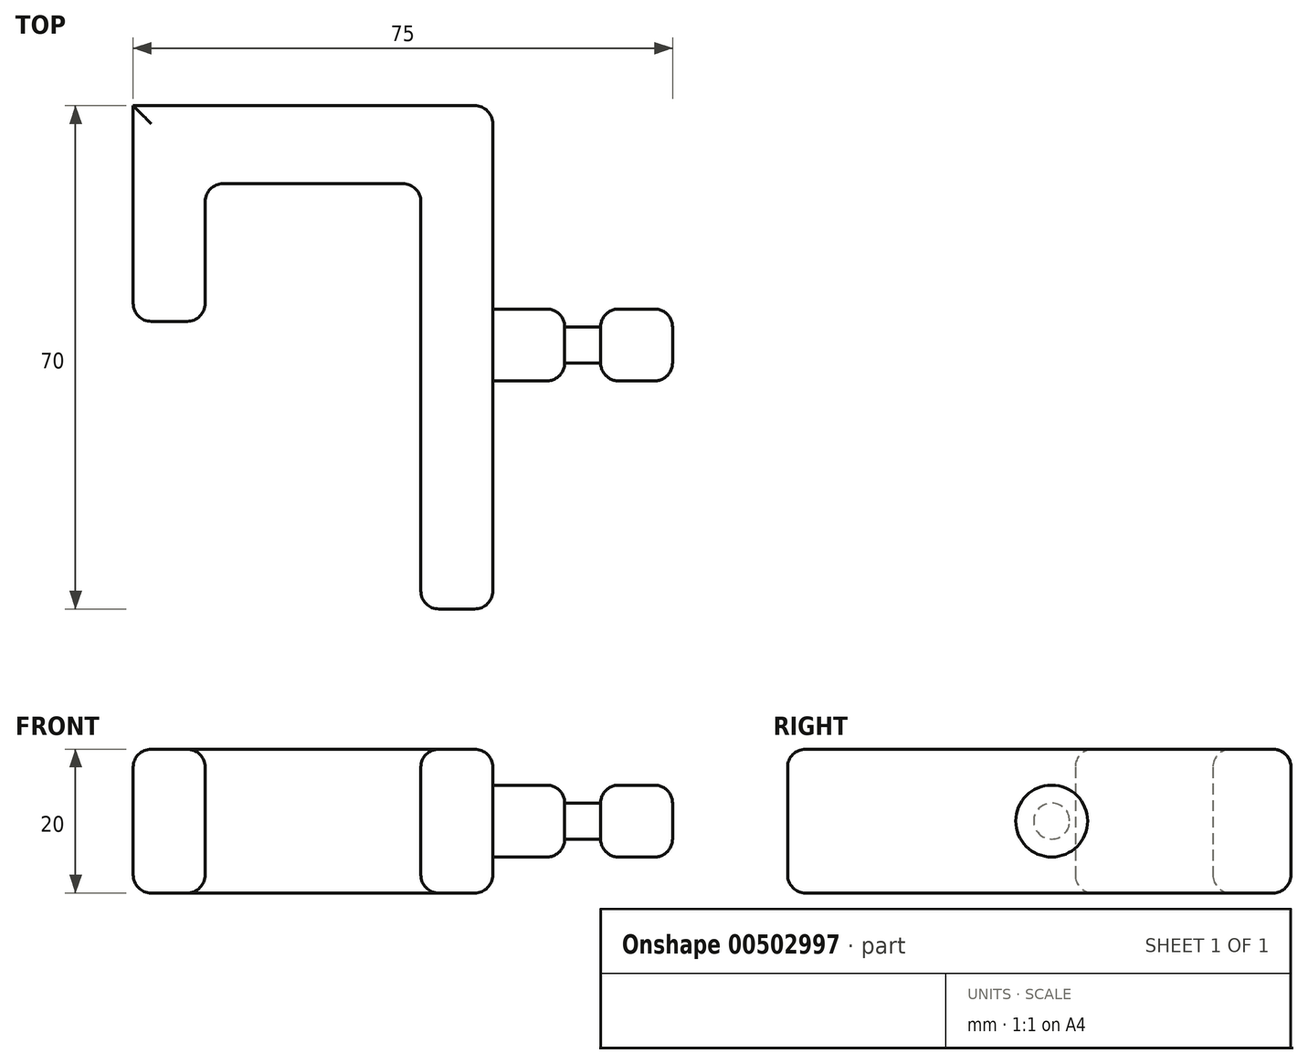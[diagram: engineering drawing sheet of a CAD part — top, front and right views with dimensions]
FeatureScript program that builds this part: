
annotation { "Feature Type Name" : "Feature", "Feature Type Description" : "" }
export const myFeature = defineFeature(function(context is Context, id is Id, definition is map)
    precondition{}
    {
        {
            var Q0;
            Q0=qCreatedBy(makeId("Top.planeOp"),FACE);
            var sketch = newSketch(context, id + "F0", { "sketchPlane" : qUnion([Q0])});
            skLineSegment(sketch, "E0.bottom", {"start": v(-50, 33.27) * mm, "end": v(-40, 33.27) * mm});
            skLineSegment(sketch, "E0.top", {"start": v(-50, 3.27) * mm, "end": v(-40, 3.27) * mm});
            skLineSegment(sketch, "E0.left", {"start": v(-50, 33.27) * mm, "end": v(-50, 3.27) * mm});
            skLineSegment(sketch, "E0.right", {"start": v(-40, 33.27) * mm, "end": v(-40, 3.27) * mm});
            skLineSegment(sketch, "E1.bottom", {"start": v(-50, 33.27) * mm, "end": v(0, 33.27) * mm});
            skLineSegment(sketch, "E1.top", {"start": v(-50, 22.42) * mm, "end": v(0, 22.42) * mm});
            skLineSegment(sketch, "E1.left", {"start": v(-50, 33.27) * mm, "end": v(-50, 22.42) * mm});
            skLineSegment(sketch, "E1.right", {"start": v(0, 33.27) * mm, "end": v(0, 22.42) * mm});
            skLineSegment(sketch, "E2.bottom", {"start": v(0, 33.27) * mm, "end": v(-10, 33.27) * mm});
            skLineSegment(sketch, "E2.top", {"start": v(0, -36.73) * mm, "end": v(-10, -36.73) * mm});
            skLineSegment(sketch, "E2.left", {"start": v(0, 33.27) * mm, "end": v(0, -36.73) * mm});
            skLineSegment(sketch, "E2.right", {"start": v(-10, 33.27) * mm, "end": v(-10, -36.73) * mm});
            skSolve(sketch);
        }
        {
            var Q0;
            Q0 = qSketchRegion(id + "F0", true);
            extrude(context, id + "F1", {"entities" : qUnion([Q0]), "depth" : 20 * mm});
        }
        {
            var Q0;
            Q0=makeQuery(id+"F1.opExtrude","SWEPT_FACE",FACE,{"disambiguationData":[OSD([sQuery(id+"F0.wireOp",EDGE,"E2.left")])]});
            var sketch = newSketch(context, id + "F2", { "sketchPlane" : qUnion([Q0])});
            skCircle(sketch, "E3", {"center": v(0, 10) * mm, "radius": 5 * mm});
            skSolve(sketch);
        }
        {
            var Q0;
            Q0=makeQuery(id+"F2.imprint","IMPRINT",FACE,{"disambiguationData":[TD([[makeQuery(id+"F2.imprint","IMPRINT",EDGE,{"derivedFrom":sQuery(id+"F2.wireOp",EDGE,"E3")}),1.0]])]});
            extrude(context, id + "F3", {"entities" : qUnion([Q0]), "operationType" : NewBodyOperationType.ADD, "depth" : 10 * mm});
        }
        {
            var Q0;
            Q0=makeQuery(id+"F3.opExtrude","CAP_FACE",FACE,{"disambiguationData":[OSD([sQuery(id+"F2.wireOp",EDGE,"E3")])],"isStart":false});
            var sketch = newSketch(context, id + "F4", { "sketchPlane" : qUnion([Q0])});
            skSolve(sketch);
        }
        {
            var Q0;
            Q0=makeQuery(id+"F4.imprint","IMPRINT",FACE,{"disambiguationData":[TD([[makeQuery(id+"F4.imprint","IMPRINT",EDGE,{"derivedFrom":makeQuery(id+"F3.opExtrude","CAP_EDGE",EDGE,{"disambiguationData":[OSD([sQuery(id+"F2.wireOp",EDGE,"E3")])],"isStart":false})}),1.0]])]});
            var sketch = newSketch(context, id + "F5", { "sketchPlane" : qUnion([Q0])});
            skCircle(sketch, "E4", {"center": v(0, 10) * mm, "radius": 2.5 * mm});
            skSolve(sketch);
        }
        {
            var Q0;
            Q0=makeQuery(id+"F5.imprint","IMPRINT",FACE,{"disambiguationData":[TD([[makeQuery(id+"F5.imprint","IMPRINT",EDGE,{"derivedFrom":sQuery(id+"F5.wireOp",EDGE,"E4")}),1.0]])]});
            extrude(context, id + "F6", {"entities" : qUnion([Q0]), "operationType" : NewBodyOperationType.ADD, "depth" : 5 * mm});
        }
        {
            var Q0;
            Q0=makeQuery(id+"F6.opExtrude","CAP_FACE",FACE,{"disambiguationData":[OSD([sQuery(id+"F5.wireOp",EDGE,"E4")])],"isStart":false});
            var sketch = newSketch(context, id + "F7", { "sketchPlane" : qUnion([Q0])});
            skCircle(sketch, "E5", {"center": v(0, 10) * mm, "radius": 5 * mm});
            skSolve(sketch);
        }
        {
            var Q0;
            Q0=makeQuery(id+"F7.imprint","IMPRINT",FACE,{"disambiguationData":[TD([[makeQuery(id+"F7.imprint","IMPRINT",EDGE,{"derivedFrom":sQuery(id+"F7.wireOp",EDGE,"E5")}),1.0]])]});
            var Q1;
            Q1=makeQuery(id+"F7.imprint","IMPRINT",FACE,{"disambiguationData":[TD([[makeQuery(id+"F7.imprint","IMPRINT",EDGE,{"derivedFrom":makeQuery(id+"F6.opExtrude","CAP_EDGE",EDGE,{"disambiguationData":[OSD([sQuery(id+"F5.wireOp",EDGE,"E4")])],"isStart":false})}),1.0]])]});
            extrude(context, id + "F8", {"entities" : qUnion([Q0, Q1]), "operationType" : NewBodyOperationType.ADD, "depth" : 10 * mm});
        }
        {
            var Q0;
            Q0=makeQuery(id+"F1.opExtrude","SWEPT_EDGE",EDGE,{"disambiguationData":[OSD([sQuery(id+"F0.wireOp",EDGE,"E2.bottom"),sQuery(id+"F0.wireOp",EDGE,"E2.left")])]});
            var Q1;
            Q1=makeQuery(id+"F1.opExtrude","SWEPT_EDGE",EDGE,{"disambiguationData":[OSD([sQuery(id+"F0.wireOp",EDGE,"E1.bottom"),sQuery(id+"F0.wireOp",EDGE,"E1.left")])]});
            var Q2;
            Q2=makeQuery(id+"F1.opExtrude","SWEPT_EDGE",EDGE,{"disambiguationData":[OSD([sQuery(id+"F0.wireOp",EDGE,"E0.top"),sQuery(id+"F0.wireOp",EDGE,"E0.left")])]});
            var Q3;
            Q3=makeQuery(id+"F1.opExtrude","SWEPT_EDGE",EDGE,{"disambiguationData":[OSD([sQuery(id+"F0.wireOp",EDGE,"E0.top"),sQuery(id+"F0.wireOp",EDGE,"E0.right")])]});
            var Q4;
            Q4=makeQuery(id+"F1.opExtrude","SWEPT_EDGE",EDGE,{"disambiguationData":[OSD([sQuery(id+"F0.wireOp",EDGE,"E0.right"),sQuery(id+"F0.wireOp",EDGE,"E1.top")])]});
            var Q5;
            Q5=makeQuery(id+"F1.opExtrude","SWEPT_EDGE",EDGE,{"disambiguationData":[OSD([sQuery(id+"F0.wireOp",EDGE,"E1.top"),sQuery(id+"F0.wireOp",EDGE,"E2.right")])]});
            var Q6;
            Q6=makeQuery(id+"F1.opExtrude","SWEPT_EDGE",EDGE,{"disambiguationData":[OSD([sQuery(id+"F0.wireOp",EDGE,"E2.top"),sQuery(id+"F0.wireOp",EDGE,"E2.right")])]});
            var Q7;
            Q7=makeQuery(id+"F1.opExtrude","SWEPT_EDGE",EDGE,{"disambiguationData":[OSD([sQuery(id+"F0.wireOp",EDGE,"E2.top"),sQuery(id+"F0.wireOp",EDGE,"E2.left")])]});
            var Q8;
            Q8=makeQuery(id+"F1.opExtrude","CAP_EDGE",EDGE,{"disambiguationData":[OSD([sQuery(id+"F0.wireOp",EDGE,"E2.left")])],"isStart":false});
            var Q9;
            Q9=makeQuery(id+"F1.opExtrude","CAP_EDGE",EDGE,{"disambiguationData":[OSD([sQuery(id+"F0.wireOp",EDGE,"E2.right")])],"isStart":false});
            var Q10;
            Q10=makeQuery(id+"F1.opExtrude","CAP_EDGE",EDGE,{"disambiguationData":[OSD([sQuery(id+"F0.wireOp",EDGE,"E1.top")])],"isStart":true});
            var Q11;
            Q11=makeQuery(id+"F1.opExtrude","CAP_EDGE",EDGE,{"disambiguationData":[OSD([sQuery(id+"F0.wireOp",EDGE,"E0.left"),sQuery(id+"F0.wireOp",EDGE,"E1.left")])],"isStart":false});
            var Q12;
            Q12=makeQuery(id+"F1.opExtrude","CAP_EDGE",EDGE,{"disambiguationData":[OSD([sQuery(id+"F0.wireOp",EDGE,"E0.left"),sQuery(id+"F0.wireOp",EDGE,"E1.left")])],"isStart":true});
            var Q13;
            Q13=makeQuery(id+"F1.opExtrude","CAP_EDGE",EDGE,{"disambiguationData":[OSD([sQuery(id+"F0.wireOp",EDGE,"E1.bottom"),sQuery(id+"F0.wireOp",EDGE,"E2.bottom")])],"isStart":true});
            var Q14;
            Q14=makeQuery(id+"F1.opExtrude","CAP_EDGE",EDGE,{"disambiguationData":[OSD([sQuery(id+"F0.wireOp",EDGE,"E1.bottom"),sQuery(id+"F0.wireOp",EDGE,"E2.bottom")])],"isStart":false});
            var Q15;
            Q15=makeQuery(id+"F1.opExtrude","CAP_EDGE",EDGE,{"disambiguationData":[OSD([sQuery(id+"F0.wireOp",EDGE,"E2.left")])],"isStart":true});
            fillet(context, id + "F9", {"entities" : qUnion([Q0, Q1, Q2, Q3, Q4, Q5, Q6, Q7, Q8, Q9, Q10, Q11, Q12, Q13, Q14, Q15]), "radius" : 2.5 * mm, "tangentPropagation" : true, "allowEdgeOverflow" : false});
        }
        {
            var Q0;
            Q0=makeQuery(id+"F1.opExtrude","CAP_EDGE",EDGE,{"disambiguationData":[OSD([sQuery(id+"F0.wireOp",EDGE,"E0.top")])],"isStart":true});
            var Q1;
            Q1=makeQuery(id+"F1.opExtrude","CAP_EDGE",EDGE,{"disambiguationData":[OSD([sQuery(id+"F0.wireOp",EDGE,"E2.top")])],"isStart":true});
            var Q2;
            Q2=makeQuery(id+"F1.opExtrude","CAP_EDGE",EDGE,{"disambiguationData":[OSD([sQuery(id+"F0.wireOp",EDGE,"E2.top")])],"isStart":false});
            var Q3;
            Q3=makeQuery(id+"F3.opExtrude","CAP_EDGE",EDGE,{"disambiguationData":[OSD([sQuery(id+"F2.wireOp",EDGE,"E3")])],"isStart":true});
            var Q4;
            Q4=makeQuery(id+"F8.opExtrude","CAP_EDGE",EDGE,{"disambiguationData":[OSD([sQuery(id+"F7.wireOp",EDGE,"E5")])],"isStart":false});
            var Q5;
            Q5=makeQuery(id+"F3.opExtrude","CAP_EDGE",EDGE,{"disambiguationData":[OSD([sQuery(id+"F2.wireOp",EDGE,"E3")])],"isStart":false});
            var Q6;
            Q6=makeQuery(id+"F8.opExtrude","CAP_EDGE",EDGE,{"disambiguationData":[OSD([sQuery(id+"F7.wireOp",EDGE,"E5")])],"isStart":true});
            fillet(context, id + "F10", {"entities" : qUnion([Q0, Q1, Q2, Q3, Q4, Q5, Q6]), "radius" : 2.5 * mm, "tangentPropagation" : true, "allowEdgeOverflow" : false});
        }
        {
            var Q0;
            Q0=makeQuery(id+"F1.opExtrude","CAP_EDGE",EDGE,{"disambiguationData":[OSD([sQuery(id+"F0.wireOp",EDGE,"E0.top")])],"isStart":false});
            fillet(context, id + "F11", {"entities" : qUnion([Q0]), "radius" : 2.5 * mm, "tangentPropagation" : true, "allowEdgeOverflow" : false});
        }
    });
